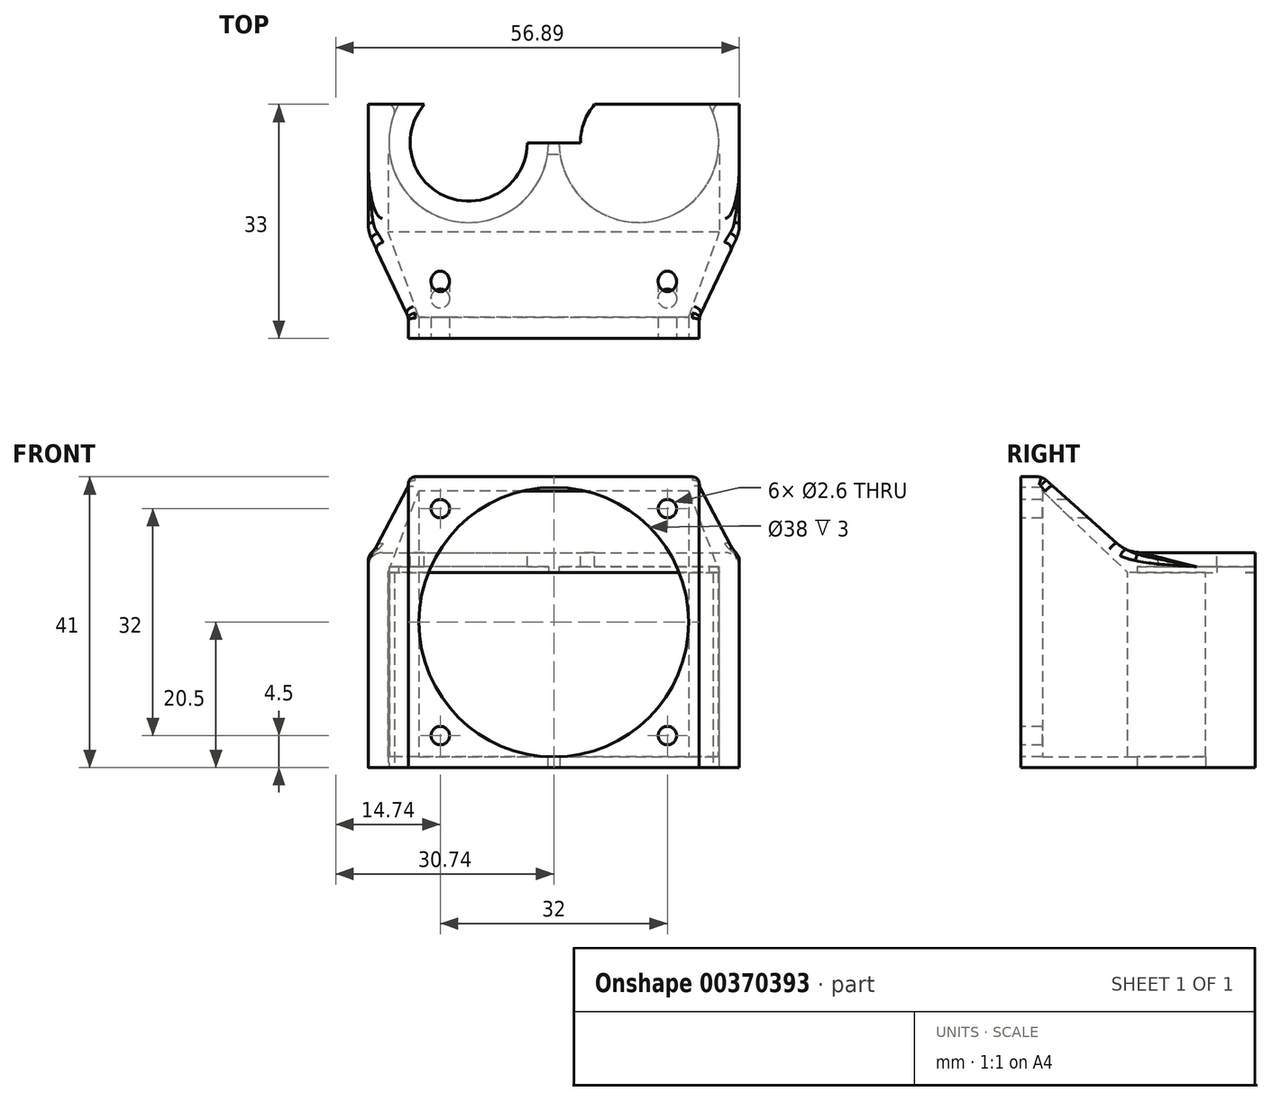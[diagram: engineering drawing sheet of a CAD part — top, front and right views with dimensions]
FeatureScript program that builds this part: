
annotation { "Feature Type Name" : "Feature", "Feature Type Description" : "" }
export const myFeature = defineFeature(function(context is Context, id is Id, definition is map)
    precondition{}
    {
        {
            var Q0;
            Q0=qCreatedBy(makeId("Front.planeOp"),FACE);
            var sketch = newSketch(context, id + "F0", { "sketchPlane" : qUnion([Q0])});
            skLineSegment(sketch, "E0.bottom", {"start": v(23.35, -13.75) * mm, "end": v(-23.35, -13.75) * mm});
            skLineSegment(sketch, "E0.top", {"start": v(23.35, 13.75) * mm, "end": v(-23.35, 13.75) * mm});
            skLineSegment(sketch, "E0.left", {"start": v(23.35, -13.75) * mm, "end": v(23.35, 13.75) * mm});
            skLineSegment(sketch, "E0.right", {"start": v(-23.35, -13.75) * mm, "end": v(-23.35, 13.75) * mm});
            skPoint(sketch, "E0.middle", {"position": v(0, 0) * mm});
            skLineSegment(sketch, "E1.bottom", {"start": v(-26.15, 16.55) * mm, "end": v(26.15, 16.55) * mm});
            skLineSegment(sketch, "E1.top", {"start": v(-26.15, -13.75) * mm, "end": v(26.15, -13.75) * mm});
            skLineSegment(sketch, "E1.left", {"start": v(-26.15, 16.55) * mm, "end": v(-26.15, -13.75) * mm});
            skLineSegment(sketch, "E1.right", {"start": v(26.15, 16.55) * mm, "end": v(26.15, -13.75) * mm});
            skLineSegment(sketch, "E2", {"start": v(-23.35, 13.75) * mm, "end": v(-26.15, 16.55) * mm});
            skLineSegment(sketch, "E3", {"start": v(23.35, 13.75) * mm, "end": v(26.15, 16.55) * mm});
            skSolve(sketch);
        }
        {
            var Q0;
            Q0=makeQuery(id+"F0.imprint","IMPRINT",FACE,{"disambiguationData":[TD([[makeQuery(id+"F0.imprint","IMPRINT",EDGE,{"derivedFrom":sQuery(id+"F0.wireOp",EDGE,"E0.top")}),-1.0]])]});
            var Q1;
            {var subQ0=sQuery(id+"F0.wireOp",EDGE,"E0.left");Q1=makeQuery(id+"F0.imprint","IMPRINT",FACE,{"disambiguationData":[TD([[makeQuery(id+"F0.imprint","IMPRINT",EDGE,{"derivedFrom":subQ0}),-1.0]])]});}
            var Q2;
            {var subQ0=sQuery(id+"F0.wireOp",EDGE,"E0.right");Q2=makeQuery(id+"F0.imprint","IMPRINT",FACE,{"disambiguationData":[TD([[makeQuery(id+"F0.imprint","IMPRINT",EDGE,{"derivedFrom":subQ0}),1.0]])]});}
            extrude(context, id + "F1", {"entities" : qUnion([Q0, Q1, Q2]), "oppositeDirection" : true, "depth" : 18 * mm, "offsetDistance" : 25 * mm});
        }
        {
            var Q0;
            Q0=makeQuery(id+"F1.opExtrude","SWEPT_FACE",FACE,{"disambiguationData":[OSD([sQuery(id+"F0.wireOp",EDGE,"E1.bottom")])]});
            var sketch = newSketch(context, id + "F2", { "sketchPlane" : qUnion([Q0])});
            skCircle(sketch, "E4", {"center": v(-12, 12.6) * mm, "radius": 8.25 * mm});
            skCircle(sketch, "E5.MirrorC", {"center": v(12, 12.6) * mm, "radius": 8.25 * mm});
            skLineSegment(sketch, "E6", {"start": v(-3.75, 12.6) * mm, "end": v(3.75, 12.6) * mm});
            skSolve(sketch);
        }
        {
            var Q0;
            Q0=makeQuery(id+"F2.imprint","IMPRINT",FACE,{"disambiguationData":[TD([[makeQuery(id+"F2.imprint","IMPRINT",EDGE,{"derivedFrom":sQuery(id+"F2.wireOp",EDGE,"E4")}),1.0]])]});
            var Q1;
            Q1=makeQuery(id+"F2.imprint","IMPRINT",FACE,{"disambiguationData":[TD([[makeQuery(id+"F2.imprint","IMPRINT",EDGE,{"derivedFrom":sQuery(id+"F2.wireOp",EDGE,"E5.MirrorC")}),-1.0]])]});
            var Q2;
            {var subQ0=sQuery(id+"F2.wireOp",EDGE,"E6");Q2=makeQuery(id+"F2.imprint","IMPRINT",FACE,{"disambiguationData":[TD([[makeQuery(id+"F2.imprint","IMPRINT",EDGE,{"derivedFrom":subQ0}),1.0]])]});}
            extrude(context, id + "F3", {"entities" : qUnion([Q0, Q1, Q2]), "operationType" : NewBodyOperationType.REMOVE, "oppositeDirection" : true, "depth" : 25 * mm, "offsetDistance" : 25 * mm});
        }
        {
            var Q0;
            Q0=qCreatedBy(makeId("Front.planeOp"),FACE);
            cPlane(context, id + "F4", {"entities" : qUnion([Q0]), "cplaneType" : CPlaneType.OFFSET, "offset" : 15 * mm, "width" : 150 * mm, "height" : 150 * mm});
        }
        {
            var Q0;
            Q0=qCreatedBy(id+"F4.planeOp",FACE);
            var sketch = newSketch(context, id + "F5", { "sketchPlane" : qUnion([Q0])});
            skLineSegment(sketch, "E7.bottom", {"start": v(-26.15, -13.75) * mm, "end": v(26.15, -13.75) * mm, "construction": true});
            skLineSegment(sketch, "E7.top", {"start": v(-26.15, 16.55) * mm, "end": v(26.15, 16.55) * mm, "construction": true});
            skLineSegment(sketch, "E7.left", {"start": v(-26.15, -13.75) * mm, "end": v(-26.15, 16.55) * mm, "construction": true});
            skLineSegment(sketch, "E7.right", {"start": v(26.15, -13.75) * mm, "end": v(26.15, 16.55) * mm, "construction": true});
            skLineSegment(sketch, "E8.bottom", {"start": v(-20.5, -13.75) * mm, "end": v(20.5, -13.75) * mm});
            skLineSegment(sketch, "E8.top", {"start": v(-20.5, 27.25) * mm, "end": v(20.5, 27.25) * mm});
            skLineSegment(sketch, "E8.left", {"start": v(-20.5, -13.75) * mm, "end": v(-20.5, 27.25) * mm});
            skLineSegment(sketch, "E8.right", {"start": v(20.5, -13.75) * mm, "end": v(20.5, 27.25) * mm});
            skPoint(sketch, "E9.centerSnap0", {"position": v(-20.5, 6.75) * mm});
            skSolve(sketch);
        }
        {
            var Q0;
            Q0=makeQuery(id+"F5.imprint","IMPRINT",FACE,{"disambiguationData":[TD([[makeQuery(id+"F5.imprint","IMPRINT",EDGE,{"derivedFrom":sQuery(id+"F5.wireOp",EDGE,"E8.bottom")}),1.0]])]});
            extrude(context, id + "F6", {"entities" : qUnion([Q0]), "oppositeDirection" : true, "depth" : 3 * mm, "offsetDistance" : 25 * mm});
        }
        {
            var Q0;
            Q0=makeQuery(id+"F6.opExtrude","CAP_FACE",FACE,{"disambiguationData":[OSD([sQuery(id+"F5.wireOp",EDGE,"E8.bottom"),sQuery(id+"F5.wireOp",EDGE,"E8.top"),sQuery(id+"F5.wireOp",EDGE,"E8.left"),sQuery(id+"F5.wireOp",EDGE,"E8.right")])],"isStart":false});
            var sketch = newSketch(context, id + "F7", { "sketchPlane" : qUnion([Q0])});
            skLineSegment(sketch, "E10.bottom", {"start": v(-19, 25.25) * mm, "end": v(19, 25.25) * mm});
            skLineSegment(sketch, "E10.top", {"start": v(-19, -13.75) * mm, "end": v(19, -13.75) * mm});
            skLineSegment(sketch, "E10.left", {"start": v(-19, 25.25) * mm, "end": v(-19, -13.75) * mm});
            skLineSegment(sketch, "E10.right", {"start": v(19, 25.25) * mm, "end": v(19, -13.75) * mm});
            skLineSegment(sketch, "E11", {"start": v(-19, 25.25) * mm, "end": v(-20.5, 27.25) * mm});
            skLineSegment(sketch, "E12", {"start": v(20.5, 27.25) * mm, "end": v(19, 25.25) * mm});
            skSolve(sketch);
        }
        {
            var Q0;
            {var subQ0=sQuery(id+"F7.wireOp",EDGE,"E10.left");Q0=makeQuery(id+"F7.imprint","IMPRINT",FACE,{"disambiguationData":[TD([[makeQuery(id+"F7.imprint","IMPRINT",EDGE,{"derivedFrom":subQ0}),-1.0]])]});}
            var Q1;
            {var subQ0=sQuery(id+"F0.wireOp",EDGE,"E0.left");Q1=makeQuery(id+"F0.imprint","IMPRINT",FACE,{"disambiguationData":[TD([[makeQuery(id+"F0.imprint","IMPRINT",EDGE,{"derivedFrom":subQ0}),-1.0]])]});}
            loft(context, id + "F8", {"operationType" : NewBodyOperationType.ADD, "sheetProfilesArray" : [{ "sheetProfileEntities" : qUnion([Q0]) }, { "sheetProfileEntities" : qUnion([Q1]) }]});
        }
        {
            var Q1;
            {var subQ0=sQuery(id+"F0.wireOp",EDGE,"E0.right");Q1=makeQuery(id+"F0.imprint","IMPRINT",FACE,{"disambiguationData":[TD([[makeQuery(id+"F0.imprint","IMPRINT",EDGE,{"derivedFrom":subQ0}),1.0]])]});}
            var Q2;
            {var subQ0=sQuery(id+"F7.wireOp",EDGE,"E10.right");Q2=makeQuery(id+"F7.imprint","IMPRINT",FACE,{"disambiguationData":[TD([[makeQuery(id+"F7.imprint","IMPRINT",EDGE,{"derivedFrom":subQ0}),1.0]])]});}
            loft(context, id + "F9", {"operationType" : NewBodyOperationType.ADD, "sheetProfilesArray" : [{ "sheetProfileEntities" : qUnion([Q1]) }, { "sheetProfileEntities" : qUnion([Q2]) }]});
        }
        {
            var Q1;
            Q1=makeQuery(id+"F7.imprint","IMPRINT",FACE,{"disambiguationData":[TD([[makeQuery(id+"F7.imprint","IMPRINT",EDGE,{"derivedFrom":sQuery(id+"F7.wireOp",EDGE,"E10.bottom")}),1.0]])]});
            var Q2;
            Q2=makeQuery(id+"F0.imprint","IMPRINT",FACE,{"disambiguationData":[TD([[makeQuery(id+"F0.imprint","IMPRINT",EDGE,{"derivedFrom":sQuery(id+"F0.wireOp",EDGE,"E0.top")}),-1.0]])]});
            loft(context, id + "F10", {"operationType" : NewBodyOperationType.ADD, "sheetProfilesArray" : [{ "sheetProfileEntities" : qUnion([Q1]) }, { "sheetProfileEntities" : qUnion([Q2]) }]});
        }
        {
            var Q0;
            Q0=makeQuery(id+"F6.opExtrude","CAP_FACE",FACE,{"disambiguationData":[OSD([sQuery(id+"F5.wireOp",EDGE,"E8.bottom"),sQuery(id+"F5.wireOp",EDGE,"E8.top"),sQuery(id+"F5.wireOp",EDGE,"E8.left"),sQuery(id+"F5.wireOp",EDGE,"E8.right")])],"isStart":true});
            var sketch = newSketch(context, id + "F11", { "sketchPlane" : qUnion([Q0])});
            skCircle(sketch, "E13", {"center": v(0, 6.75) * mm, "radius": 19 * mm});
            skLineSegment(sketch, "E14", {"start": v(-20.5, 6.75) * mm, "end": v(20.5, 6.75) * mm, "construction": true});
            skLineSegment(sketch, "E15", {"start": v(0, 27.25) * mm, "end": v(0, -13.75) * mm, "construction": true});
            skPoint(sketch, "E16", {"position": v(-16, 22.75) * mm});
            skPoint(sketch, "E17.MirrorP", {"position": v(16, 22.75) * mm});
            skPoint(sketch, "E18.MirrorP", {"position": v(-16, -9.25) * mm});
            skPoint(sketch, "E19.MirrorP", {"position": v(16, -9.25) * mm});
            skSolve(sketch);
        }
        {
            var Q0;
            Q0=sQuery(id+"F11.wireOp",VERTEX,"E16");
            var Q1;
            Q1=sQuery(id+"F11.wireOp",VERTEX,"E17.MirrorP");
            var Q2;
            Q2=sQuery(id+"F11.wireOp",VERTEX,"E19.MirrorP");
            var Q3;
            Q3=sQuery(id+"F11.wireOp",VERTEX,"E18.MirrorP");
            var Q4;
            Q4=makeQuery(id+"F1.opExtrude","SWEPT_BODY",BODY,{"disambiguationData":[OSD([sQuery(id+"F0.wireOp",EDGE,"E0.top"),sQuery(id+"F0.wireOp",EDGE,"E0.left"),sQuery(id+"F0.wireOp",EDGE,"E0.right"),sQuery(id+"F0.wireOp",EDGE,"E1.bottom"),sQuery(id+"F0.wireOp",EDGE,"E1.top"),sQuery(id+"F0.wireOp",EDGE,"E1.left"),sQuery(id+"F0.wireOp",EDGE,"E1.right")])]});
            hole(context, id + "F12", {"style" : HoleStyle.SIMPLE, "endStyle" : HoleEndStyle.BLIND, "holeDiameter" : 2.6 * mm, "majorDiameter" : 5 * mm, "holeDepth" : 10 * mm, "isTappedThrough" : true, "tappedDepth" : 12 * mm, "tapClearance" : 3, "locations" : qUnion([Q0, Q1, Q2, Q3]), "scope" : qUnion([Q4])});
        }
        {
            var Q0;
            Q0 = qSketchRegion(id + "F11", true);
            var Q1;
            Q1=makeQuery(id+"F6.opExtrude","CAP_FACE",FACE,{"disambiguationData":[OSD([sQuery(id+"F5.wireOp",EDGE,"E8.bottom"),sQuery(id+"F5.wireOp",EDGE,"E8.top"),sQuery(id+"F5.wireOp",EDGE,"E8.left"),sQuery(id+"F5.wireOp",EDGE,"E8.right")])],"isStart":false});
            extrude(context, id + "F13", {"entities" : qUnion([Q0]), "operationType" : NewBodyOperationType.REMOVE, "endBound" : BoundingType.UP_TO_SURFACE, "oppositeDirection" : true, "depth" : 25 * mm, "endBoundEntityFace" : qUnion([Q1]), "offsetDistance" : 25 * mm});
        }
        {
            var Q0;
            {var subQ0=sQuery(id+"F7.wireOp",EDGE,"E10.top");var subQ1=sQuery(id+"F5.wireOp",EDGE,"E8.bottom");var subQ2=sQuery(id+"F0.wireOp",EDGE,"E1.left");var subQ3=sQuery(id+"F0.wireOp",EDGE,"E1.top");var subQ4=sQuery(id+"F0.wireOp",EDGE,"E0.right");var subQ5=sQuery(id+"F0.wireOp",EDGE,"E1.right");var subQ6=sQuery(id+"F0.wireOp",EDGE,"E0.left");Q0=makeQuery(id+"F9.boolean.opBoolean","MERGE",FACE,{"derivedFrom":[makeQuery(id+"F1.opExtrude","SWEPT_FACE",FACE,{"disambiguationData":[OSD([subQ3]),TDD([makeQuery(id+"F0.imprint","IMPRINT",EDGE,{"disambiguationData":[TD([[makeQuery(id+"F0.imprint","INTERSECT",VERTEX,{"derivedFrom":[subQ4,subQ3]}),1.0]])],"derivedFrom":subQ3})])]}),makeQuery(id+"F8.boolean.opBoolean","MERGE",FACE,{"derivedFrom":[makeQuery(id+"F1.opExtrude","SWEPT_FACE",FACE,{"disambiguationData":[OSD([subQ3]),TDD([makeQuery(id+"F0.imprint","IMPRINT",EDGE,{"disambiguationData":[TD([[makeQuery(id+"F0.imprint","INTERSECT",VERTEX,{"derivedFrom":[subQ6,subQ3]}),-1.0]])],"derivedFrom":subQ3})])]}),makeQuery(id+"F6.opExtrude","SWEPT_FACE",FACE,{"disambiguationData":[OSD([subQ1])]}),makeQuery(id+"F8.opLoft","SWEPT_FACE",FACE,{"disambiguationData":[OSD([subQ6,subQ3,subQ5,subQ1,sQuery(id+"F5.wireOp",EDGE,"E8.right"),subQ0,sQuery(id+"F7.wireOp",EDGE,"E10.left")])]})]}),makeQuery(id+"F9.opLoft","SWEPT_FACE",FACE,{"disambiguationData":[OSD([subQ4,subQ3,subQ2,subQ1,sQuery(id+"F5.wireOp",EDGE,"E8.left"),subQ0,sQuery(id+"F7.wireOp",EDGE,"E10.right")])]})]});}
            var sketch = newSketch(context, id + "F14", { "sketchPlane" : qUnion([Q0])});
            skLineSegment(sketch, "E20", {"start": v(-20.5, 15) * mm, "end": v(-20.5, 12) * mm});
            skLineSegment(sketch, "E21", {"start": v(-20.5, 12) * mm, "end": v(-26.15, 0) * mm});
            skLineSegment(sketch, "E22", {"start": v(-26.15, 0) * mm, "end": v(-26.15, -11) * mm});
            skLineSegment(sketch, "E23", {"start": v(-26.15, -11) * mm, "end": v(26.15, -11) * mm});
            skLineSegment(sketch, "E24", {"start": v(26.15, -11) * mm, "end": v(26.15, 0) * mm});
            skLineSegment(sketch, "E25", {"start": v(26.15, 0) * mm, "end": v(20.5, 12) * mm});
            skLineSegment(sketch, "E26", {"start": v(20.5, 12) * mm, "end": v(20.5, 15) * mm});
            skLineSegment(sketch, "E27", {"start": v(20.5, 15) * mm, "end": v(-20.5, 15) * mm});
            skLineSegment(sketch, "E28", {"start": v(-21.15, -17.98) * mm, "end": v(-22.65, -11) * mm});
            skLineSegment(sketch, "E29.MirrorCS", {"start": v(21.15, -17.98) * mm, "end": v(22.65, -11) * mm});
            skLineSegment(sketch, "E30", {"start": v(-21.15, -17.98) * mm, "end": v(-26.15, -18) * mm});
            skLineSegment(sketch, "E31", {"start": v(-26.15, -18) * mm, "end": v(-26.15, -11) * mm});
            skLineSegment(sketch, "E32.MirrorCS", {"start": v(21.15, -17.98) * mm, "end": v(26.15, -18) * mm});
            skLineSegment(sketch, "E33.MirrorCS", {"start": v(26.15, -18) * mm, "end": v(26.15, -11) * mm});
            skSolve(sketch);
        }
        {
            var Q0;
            Q0=makeQuery(id+"F14.imprint","IMPRINT",FACE,{"disambiguationData":[TD([[makeQuery(id+"F14.imprint","IMPRINT",EDGE,{"derivedFrom":sQuery(id+"F14.wireOp",EDGE,"E20")}),-1.0]])]});
            var Q1;
            {var subQ1=sQuery(id+"F5.wireOp",EDGE,"E8.bottom");Q1=makeQuery(id+"F14.imprint","IMPRINT",FACE,{"disambiguationData":[TD([[makeQuery(id+"F14.imprint","IMPRINT",EDGE,{"derivedFrom":makeQuery(id+"F6.opExtrude","CAP_EDGE",EDGE,{"disambiguationData":[OSD([subQ1])],"isStart":false})}),-1.0]])]});}
            extrude(context, id + "F15", {"entities" : qUnion([Q0, Q1]), "operationType" : NewBodyOperationType.ADD, "oppositeDirection" : true, "depth" : 1.5 * mm, "offsetDistance" : 25 * mm});
        }
        {
            var Q0;
            {var subQ0=sQuery(id+"F14.wireOp",EDGE,"E28");Q0=makeQuery(id+"F14.imprint","IMPRINT",FACE,{"disambiguationData":[TD([[makeQuery(id+"F14.imprint","IMPRINT",EDGE,{"derivedFrom":subQ0}),1.0]])]});}
            var Q1;
            {var subQ0=sQuery(id+"F14.wireOp",EDGE,"E29.MirrorCS");Q1=makeQuery(id+"F14.imprint","IMPRINT",FACE,{"disambiguationData":[TD([[makeQuery(id+"F14.imprint","IMPRINT",EDGE,{"derivedFrom":subQ0}),-1.0]])]});}
            var Q2;
            {var subQ0=sQuery(id+"F14.wireOp",EDGE,"E33.MirrorCS");Q2=makeQuery(id+"F14.imprint","IMPRINT",FACE,{"disambiguationData":[TD([[makeQuery(id+"F14.imprint","IMPRINT",EDGE,{"derivedFrom":subQ0}),1.0]])]});}
            var Q3;
            {var subQ0=sQuery(id+"F14.wireOp",EDGE,"E31");Q3=makeQuery(id+"F14.imprint","IMPRINT",FACE,{"disambiguationData":[TD([[makeQuery(id+"F14.imprint","IMPRINT",EDGE,{"derivedFrom":subQ0}),-1.0]])]});}
            var Q4;
            Q4=makeQuery(id+"F1.opExtrude","SWEPT_FACE",FACE,{"disambiguationData":[OSD([sQuery(id+"F0.wireOp",EDGE,"E0.top")])]});
            extrude(context, id + "F16", {"entities" : qUnion([Q0, Q1, Q2, Q3]), "operationType" : NewBodyOperationType.ADD, "endBound" : BoundingType.UP_TO_SURFACE, "oppositeDirection" : true, "depth" : 25 * mm, "endBoundEntityFace" : qUnion([Q4]), "offsetDistance" : 25 * mm});
        }
        {
            var Q0;
            Q0=makeQuery(id+"F1.opExtrude","SWEPT_FACE",FACE,{"disambiguationData":[OSD([sQuery(id+"F0.wireOp",EDGE,"E0.top")])]});
            var sketch = newSketch(context, id + "F17", { "sketchPlane" : qUnion([Q0])});
            skCircle(sketch, "E34", {"center": v(-12, -12.6) * mm, "radius": 11.25 * mm});
            skCircle(sketch, "E35.MirrorC", {"center": v(12, -12.6) * mm, "radius": 11.25 * mm});
            skSolve(sketch);
        }
        {
            var Q0;
            Q0 = qSketchRegion(id + "F17", true);
            extrude(context, id + "F18", {"entities" : qUnion([Q0]), "operationType" : NewBodyOperationType.REMOVE, "oppositeDirection" : true, "depth" : .8 * mm, "offsetDistance" : 25 * mm, "hasSecondDirection" : true, "secondDirectionOppositeDirection" : false, "secondDirectionDepth" : 48.5 * mm});
        }
        {
            var Q0;
            Q0=makeQuery(id+"F18.boolean.opBoolean","INTERSECT",EDGE,{"derivedFrom":[makeQuery(id+"F16.opExtrude","SWEPT_FACE",FACE,{"disambiguationData":[OSD([sQuery(id+"F14.wireOp",EDGE,"E30")])]}),makeQuery(id+"F18.opExtrude","SWEPT_FACE",FACE,{"disambiguationData":[OSD([sQuery(id+"F17.wireOp",EDGE,"E34")])]})]});
            var Q1;
            Q1=makeQuery(id+"F18.boolean.opBoolean","INTERSECT",EDGE,{"derivedFrom":[makeQuery(id+"F16.opExtrude","SWEPT_FACE",FACE,{"disambiguationData":[OSD([sQuery(id+"F14.wireOp",EDGE,"E32.MirrorCS")])]}),makeQuery(id+"F18.opExtrude","SWEPT_FACE",FACE,{"disambiguationData":[OSD([sQuery(id+"F17.wireOp",EDGE,"E35.MirrorC")])]})]});
            fillet(context, id + "F19", {"entities" : qUnion([Q0, Q1]), "radius" : 1 * mm, "tangentPropagation" : true, "allowEdgeOverflow" : false});
        }
        {
            var Q0;
            Q0=makeQuery(id+"F1.opExtrude","SWEPT_EDGE",EDGE,{"disambiguationData":[OSD([sQuery(id+"F0.wireOp",EDGE,"E1.bottom"),sQuery(id+"F0.wireOp",EDGE,"E1.left"),sQuery(id+"F0.wireOp",EDGE,"E2")])]});
            var Q1;
            Q1=makeQuery(id+"F1.opExtrude","SWEPT_EDGE",EDGE,{"disambiguationData":[OSD([sQuery(id+"F0.wireOp",EDGE,"E1.bottom"),sQuery(id+"F0.wireOp",EDGE,"E1.right"),sQuery(id+"F0.wireOp",EDGE,"E3")])]});
            var Q2;
            {var subQ0=sQuery(id+"F5.wireOp",EDGE,"E8.top");Q2=makeQuery(id+"F10.boolean.opBoolean","MERGE",EDGE,{"derivedFrom":[makeQuery(id+"F6.opExtrude","CAP_EDGE",EDGE,{"disambiguationData":[OSD([subQ0])],"isStart":false}),makeQuery(id+"F10.opLoft","MID_CAP_EDGE",EDGE,{"disambiguationData":[OSD([subQ0,sQuery(id+"F5.wireOp",EDGE,"E8.left"),sQuery(id+"F5.wireOp",EDGE,"E8.right"),sQuery(id+"F7.wireOp",EDGE,"E11"),sQuery(id+"F7.wireOp",EDGE,"E12")])],"capPos":0.0})]});}
            var Q3;
            {var subQ0=sQuery(id+"F5.wireOp",EDGE,"E8.right");Q3=makeQuery(id+"F8.boolean.opBoolean","MERGE",EDGE,{"derivedFrom":[makeQuery(id+"F6.opExtrude","CAP_EDGE",EDGE,{"disambiguationData":[OSD([subQ0])],"isStart":false}),makeQuery(id+"F8.opLoft","MID_CAP_EDGE",EDGE,{"disambiguationData":[OSD([sQuery(id+"F5.wireOp",EDGE,"E8.bottom"),sQuery(id+"F5.wireOp",EDGE,"E8.top"),subQ0,sQuery(id+"F7.wireOp",EDGE,"E11")])],"capPos":0.0})]});}
            var Q4;
            {var subQ0=sQuery(id+"F5.wireOp",EDGE,"E8.left");Q4=makeQuery(id+"F9.boolean.opBoolean","MERGE",EDGE,{"derivedFrom":[makeQuery(id+"F6.opExtrude","CAP_EDGE",EDGE,{"disambiguationData":[OSD([subQ0])],"isStart":false}),makeQuery(id+"F9.opLoft","MID_CAP_EDGE",EDGE,{"disambiguationData":[OSD([sQuery(id+"F5.wireOp",EDGE,"E8.bottom"),sQuery(id+"F5.wireOp",EDGE,"E8.top"),subQ0,sQuery(id+"F7.wireOp",EDGE,"E12")])],"capPos":1.0})]});}
            fillet(context, id + "F20", {"entities" : qUnion([Q0, Q1, Q2, Q3, Q4]), "radius" : 2 * mm, "tangentPropagation" : true, "allowEdgeOverflow" : false});
        }
        {
            var Q0;
            {var subQ0=sQuery(id+"F0.wireOp",EDGE,"E1.bottom");Q0=makeQuery(id+"F10.boolean.opBoolean","MERGE",EDGE,{"derivedFrom":[makeQuery(id+"F1.opExtrude","CAP_EDGE",EDGE,{"disambiguationData":[OSD([subQ0])],"isStart":true}),makeQuery(id+"F10.opLoft","MID_CAP_EDGE",EDGE,{"disambiguationData":[OSD([subQ0,sQuery(id+"F0.wireOp",EDGE,"E1.left"),sQuery(id+"F0.wireOp",EDGE,"E1.right"),sQuery(id+"F0.wireOp",EDGE,"E2"),sQuery(id+"F0.wireOp",EDGE,"E3")])],"capPos":1.0})]});}
            fillet(context, id + "F21", {"entities" : qUnion([Q0]), "radius" : 5 * mm, "tangentPropagation" : true, "allowEdgeOverflow" : false});
        }
        {
            var Q0;
            {var subQ0=sQuery(id+"F0.wireOp",EDGE,"E1.left");Q0=makeQuery(id+"F9.boolean.opBoolean","MERGE",EDGE,{"derivedFrom":[makeQuery(id+"F1.opExtrude","CAP_EDGE",EDGE,{"disambiguationData":[OSD([subQ0])],"isStart":true}),makeQuery(id+"F9.opLoft","MID_CAP_EDGE",EDGE,{"disambiguationData":[OSD([sQuery(id+"F0.wireOp",EDGE,"E1.bottom"),sQuery(id+"F0.wireOp",EDGE,"E1.top"),subQ0,sQuery(id+"F0.wireOp",EDGE,"E2")])],"capPos":0.0})]});}
            var Q1;
            {var subQ0=sQuery(id+"F0.wireOp",EDGE,"E1.right");Q1=makeQuery(id+"F8.boolean.opBoolean","MERGE",EDGE,{"derivedFrom":[makeQuery(id+"F1.opExtrude","CAP_EDGE",EDGE,{"disambiguationData":[OSD([subQ0])],"isStart":true}),makeQuery(id+"F8.opLoft","MID_CAP_EDGE",EDGE,{"disambiguationData":[OSD([sQuery(id+"F0.wireOp",EDGE,"E1.bottom"),sQuery(id+"F0.wireOp",EDGE,"E1.top"),subQ0,sQuery(id+"F0.wireOp",EDGE,"E3")])],"capPos":1.0})]});}
            fillet(context, id + "F22", {"entities" : qUnion([Q0, Q1]), "radius" : 5 * mm, "tangentPropagation" : true, "allowEdgeOverflow" : false});
        }
        {
            var Q0;
            {var subQ0=sQuery(id+"F7.wireOp",EDGE,"E11");var subQ1=sQuery(id+"F5.wireOp",EDGE,"E8.right");var subQ2=sQuery(id+"F5.wireOp",EDGE,"E8.top");var subQ3=sQuery(id+"F0.wireOp",EDGE,"E3");var subQ4=sQuery(id+"F0.wireOp",EDGE,"E1.right");var subQ5=sQuery(id+"F0.wireOp",EDGE,"E1.bottom");Q0=makeQuery(id+"F10.boolean.opBoolean","MERGE",EDGE,{"derivedFrom":[makeQuery(id+"F8.opLoft","SWEPT_EDGE",EDGE,{"disambiguationData":[OSD([subQ5,subQ4,subQ3,subQ2,subQ1,subQ0])]}),makeQuery(id+"F10.opLoft","SWEPT_EDGE",EDGE,{"disambiguationData":[OSD([subQ5,subQ4,subQ3,subQ2,subQ1,subQ0])]})]});}
            var Q1;
            {var subQ0=sQuery(id+"F7.wireOp",EDGE,"E12");var subQ1=sQuery(id+"F5.wireOp",EDGE,"E8.left");var subQ2=sQuery(id+"F5.wireOp",EDGE,"E8.top");var subQ3=sQuery(id+"F0.wireOp",EDGE,"E2");var subQ4=sQuery(id+"F0.wireOp",EDGE,"E1.left");var subQ5=sQuery(id+"F0.wireOp",EDGE,"E1.bottom");Q1=makeQuery(id+"F10.boolean.opBoolean","MERGE",EDGE,{"derivedFrom":[makeQuery(id+"F9.opLoft","SWEPT_EDGE",EDGE,{"disambiguationData":[OSD([subQ5,subQ4,subQ3,subQ2,subQ1,subQ0])]}),makeQuery(id+"F10.opLoft","SWEPT_EDGE",EDGE,{"disambiguationData":[OSD([subQ5,subQ4,subQ3,subQ2,subQ1,subQ0])]})]});}
            fillet(context, id + "F23", {"entities" : qUnion([Q0, Q1]), "radius" : 1 * mm, "tangentPropagation" : true, "allowEdgeOverflow" : false});
        }
    });
